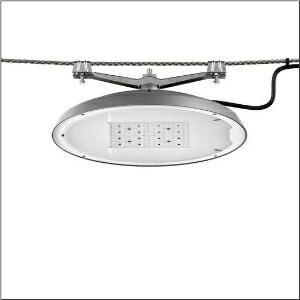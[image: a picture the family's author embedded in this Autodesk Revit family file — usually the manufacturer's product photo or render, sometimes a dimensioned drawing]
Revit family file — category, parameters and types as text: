
# Revit family: dl_50_iq_mini___st1_0s_5xa248w41f08me_1d6e
name_source: partatom
category: Lighting Fixtures
units: mm (PartAtom-declared; Revit-internal decimal feet)

## family parameters
Cut with Voids When Loaded = No
Host = Face
Light Source = No
Part Type = Normal
Room Calculation Point = No
Round Connector Dimension = Use Diameter
Shared = No

## types (1)
- --- (1 x LED, 15660 lm, 101.7 W, 4000K)
    Apparent Load = 102 VA
    CIE Flux Codes = 37 72 97 100 100
    Color Rendering = 70
    Color Temperature = 4000K
    Default Elevation = 1800 mm
    Description = DL 50 iQ mini, catenary luminaire, primary light control with lens, of PMMA, primary optical cover: cover, of toughened safety glass, transparent, light distribution: ST1.0s, light emission: direct distribution, primary light characteristic: symmetric, installation type: suspended mounting, LED, High Power LED, rated luminous flux: 15.660lm, luminous efficacy: 154lm/W, light colour: 740, colour temperature: 4000K, control gear: iQ Street-Remote, control: optimised constant luminous flux control (CLO 2.0), Desk-Remote (wireless, voltage-free reading and setting of iQ features in the workshop via application-optimized NFC function/RFID function), Light-Fading, Smart-Wire, Night-Set, Lumen-Switch, Temp-Guard, Auto-Match, Street-Remote, mains connection: 230..240V, AC, 50/60Hz, start of lifetime: 102W, end of service life: 111W, reduction: 45W, luminaire housing, of diecast aluminium, powder-coated, SITECO metallic grey (DB 702S), diameter: 500mm, height: 115mm, mounting height: 4..12m, protection rating (complete): IP66, insulation class (complete): insulation class II (safety insulation), certification: CE, ENEC, ENEC+, VDE, impact resistance: IK08, permissible operating ambient temperature for outdoor applications: -25..+40°C, standard-compliant lighting for roads and squares, packaging unit: 1 piece

Light Distribution: ST1.0s
    Height = 124 mm  [stored 0.406824 ft]
    Lamp = 1 x LED
    Lamp Light Flux = 15660 lm
    Lamp Power = 101.7 W
    Lamp count = 1
    Length = 500 mm
    Luminous efficacy = 154 lm/W
    Manufacturer = Siteco
    ModVariant = No
    Model = 5XA248W41F08ME
    Number of Poles = 1
    OnlyDefault = Yes
    Power Factor = 1
    Product Name = DL 50 iQ mini | ST1.0s
    Product group = catenary luminaire
    ProductGroupID = 6300
    Protection Class = Protection class II
    Protection Degree = IP 66
    RLX_Detail_Level = 1
    RLX_Emergency_Light_Flux = 0 lm
    RLX_Emergency_Type = 0
    RLX_Emergency_Type_DB = No
    RlxData = <blob elided: 127421 chars, md5=b4e381d9>
    Socket = socket
    Standby Power = 0 W
    System Light Flux = 15660 lm
    System Power = 102 W
    Type Comments = factory setting: luminous flux: 100 % | dim-lin: 254 | 534 mA
    Type Image = l_1251783.jpg
    URL = http://relux.com
    VarID = @adj_139869
    Voltage = 0 V
    Weight = 0.00 kg
    Width = 0 mm  [stored 0 ft]

note: [stored X ft] marks values corroborated as IEEE doubles in the binary element streams (Revit-internal decimal feet)

## geometry (parser evidence)
native form markers: Blend x4, Sweep x13
no freeform markers — native parametric forms only
